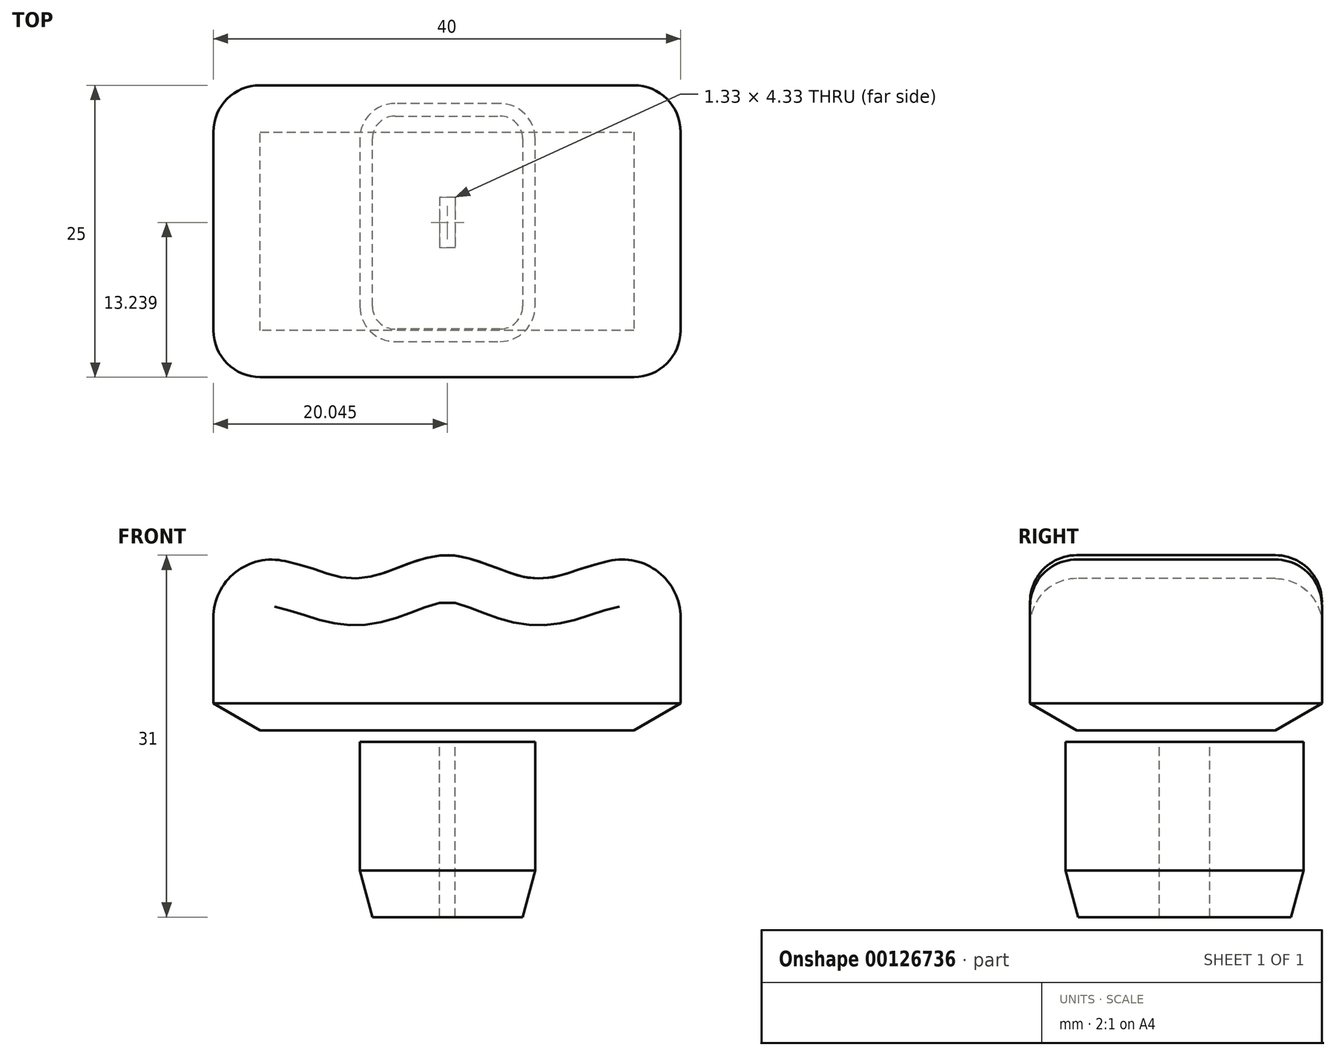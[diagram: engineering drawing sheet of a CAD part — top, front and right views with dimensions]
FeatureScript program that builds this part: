
annotation { "Feature Type Name" : "Feature", "Feature Type Description" : "" }
export const myFeature = defineFeature(function(context is Context, id is Id, definition is map)
    precondition{}
    {
        {
            var Q0;
            Q0=qCreatedBy(makeId("Front.planeOp"),FACE);
            var sketch = newSketch(context, id + "F0", { "sketchPlane" : qUnion([Q0])});
            skPoint(sketch, "E0.MirrorCS.start.orphan", {"position": v(0, 0) * mm});
            skPoint(sketch, "E1.MirrorCS.end.orphan", {"position": v(-8, 0) * mm});
            skPoint(sketch, "E2.MirrorCS.end.orphan", {"position": v(-24, 0) * mm});
            skPoint(sketch, "E2.MirrorCS.start.orphan", {"position": v(-16, 0) * mm});
            skPoint(sketch, "E3.MirrorCS.end.orphan", {"position": v(24, 0) * mm});
            skLineSegment(sketch, "E4", {"start": v(-24, 0) * mm, "end": v(-24, -14) * mm});
            skLineSegment(sketch, "E5", {"start": v(-24, -14) * mm, "end": v(16, -14) * mm});
            skLineSegment(sketch, "E6", {"start": v(16, -14) * mm, "end": v(16, 0) * mm});
            skPoint(sketch, "E7.MirrorCS.end.orphan", {"position": v(8, 0) * mm});
            skLineSegment(sketch, "E8", {"start": v(-24, 0) * mm, "end": v(-16, 0) * mm, "construction": true});
            skLineSegment(sketch, "E9", {"start": v(-16, 0) * mm, "end": v(-8, 0) * mm, "construction": true});
            skLineSegment(sketch, "E10", {"start": v(-8, 0) * mm, "end": v(0, 0) * mm, "construction": true});
            skLineSegment(sketch, "E11", {"start": v(0, 0) * mm, "end": v(8, 0) * mm, "construction": true});
            skLineSegment(sketch, "E12", {"start": v(8, 0) * mm, "end": v(16, 0) * mm, "construction": true});
            skLineSegment(sketch, "E13", {"start": v(-20, 0) * mm, "end": v(-20, 1) * mm, "construction": true});
            skLineSegment(sketch, "E14", {"start": v(-12, 0) * mm, "end": v(-12, -1) * mm, "construction": true});
            skLineSegment(sketch, "E15", {"start": v(-4, 0) * mm, "end": v(-4, 1) * mm, "construction": true});
            skLineSegment(sketch, "E16", {"start": v(4, 0) * mm, "end": v(4, -1) * mm, "construction": true});
            skPoint(sketch, "E16.endSnap0", {"position": v(4, 0) * mm});
            skLineSegment(sketch, "E17", {"start": v(12, 0) * mm, "end": v(12, 1) * mm, "construction": true});
            skFitSpline(sketch, "E18", {"points": [v(-24, 0) * mm, v(-20, 1) * mm, v(-16, 0) * mm, v(-12, -1) * mm, v(-8, 0) * mm, v(-4, 1) * mm, v(0, 0) * mm, v(4, -1) * mm, v(8, 0) * mm, v(12, 1) * mm, v(16, 0) * mm], "startDerivative": vector(5.73, 62.47) * mm, "endDerivative": vector(6.75, -59.62) * mm});
            skSolve(sketch);
        }
        {
            var Q0;
            Q0=makeQuery(id+"F0.imprint","IMPRINT",FACE,{"disambiguationData":[TD([[makeQuery(id+"F0.imprint","IMPRINT",EDGE,{"derivedFrom":sQuery(id+"F0.wireOp",EDGE,"E4")}),1.0]])]});
            extrude(context, id + "F1", {"entities" : qUnion([Q0]), "depth" : 25 * mm});
        }
        {
            var Q0;
            Q0=makeQuery(id+"F1.opExtrude","SWEPT_EDGE",EDGE,{"disambiguationData":[OSD([sQuery(id+"F0.wireOp",EDGE,"E4"),sQuery(id+"F0.wireOp",EDGE,"E18")])]});
            var Q1;
            Q1=makeQuery(id+"F1.opExtrude","SWEPT_EDGE",EDGE,{"disambiguationData":[OSD([sQuery(id+"F0.wireOp",EDGE,"E6"),sQuery(id+"F0.wireOp",EDGE,"E18")])]});
            fillet(context, id + "F2", {"entities" : qUnion([Q0, Q1]), "radius" : 5 * mm, "tangentPropagation" : true, "allowEdgeOverflow" : false});
        }
        {
            var Q0;
            Q0=makeQuery(id+"F1.opExtrude","CAP_EDGE",EDGE,{"disambiguationData":[OSD([sQuery(id+"F0.wireOp",EDGE,"E18")])],"isStart":false});
            var Q1;
            {var subQ0=sQuery(id+"F0.wireOp",EDGE,"E18");var subQ1=sQuery(id+"F0.wireOp",EDGE,"E4");Q1=makeQuery(id+"F2.opFillet","BLEND_EDGE",EDGE,{"blendedFrom":[makeQuery(id+"F1.opExtrude","SWEPT_EDGE",EDGE,{"disambiguationData":[OSD([subQ1,subQ0])]}),makeQuery(id+"F1.opExtrude","CAP_FACE",FACE,{"disambiguationData":[OSD([subQ1,sQuery(id+"F0.wireOp",EDGE,"E5"),sQuery(id+"F0.wireOp",EDGE,"E6"),subQ0])],"isStart":false})],"blendedInto":[makeQuery(id+"F1.opExtrude","CAP_FACE",FACE,{"disambiguationData":[OSD([subQ1,sQuery(id+"F0.wireOp",EDGE,"E5"),sQuery(id+"F0.wireOp",EDGE,"E6"),subQ0])],"isStart":false})]});}
            var Q2;
            {var subQ0=sQuery(id+"F0.wireOp",EDGE,"E18");var subQ1=sQuery(id+"F0.wireOp",EDGE,"E6");Q2=makeQuery(id+"F2.opFillet","BLEND_EDGE",EDGE,{"blendedFrom":[makeQuery(id+"F1.opExtrude","SWEPT_EDGE",EDGE,{"disambiguationData":[OSD([subQ1,subQ0])]}),makeQuery(id+"F1.opExtrude","CAP_FACE",FACE,{"disambiguationData":[OSD([sQuery(id+"F0.wireOp",EDGE,"E4"),sQuery(id+"F0.wireOp",EDGE,"E5"),subQ1,subQ0])],"isStart":false})],"blendedInto":[makeQuery(id+"F1.opExtrude","CAP_FACE",FACE,{"disambiguationData":[OSD([sQuery(id+"F0.wireOp",EDGE,"E4"),sQuery(id+"F0.wireOp",EDGE,"E5"),subQ1,subQ0])],"isStart":false})]});}
            fillet(context, id + "F3", {"entities" : qUnion([Q0, Q1, Q2]), "radius" : 4 * mm, "tangentPropagation" : true, "allowEdgeOverflow" : false});
        }
        {
            var Q0;
            Q0=makeQuery(id+"F1.opExtrude","CAP_EDGE",EDGE,{"disambiguationData":[OSD([sQuery(id+"F0.wireOp",EDGE,"E18")])],"isStart":true});
            var Q1;
            {var subQ0=sQuery(id+"F0.wireOp",EDGE,"E18");var subQ1=sQuery(id+"F0.wireOp",EDGE,"E4");Q1=makeQuery(id+"F2.opFillet","BLEND_EDGE",EDGE,{"blendedFrom":[makeQuery(id+"F1.opExtrude","SWEPT_EDGE",EDGE,{"disambiguationData":[OSD([subQ1,subQ0])]}),makeQuery(id+"F1.opExtrude","CAP_FACE",FACE,{"disambiguationData":[OSD([subQ1,sQuery(id+"F0.wireOp",EDGE,"E5"),sQuery(id+"F0.wireOp",EDGE,"E6"),subQ0])],"isStart":true})],"blendedInto":[makeQuery(id+"F1.opExtrude","CAP_FACE",FACE,{"disambiguationData":[OSD([subQ1,sQuery(id+"F0.wireOp",EDGE,"E5"),sQuery(id+"F0.wireOp",EDGE,"E6"),subQ0])],"isStart":true})]});}
            var Q2;
            Q2=makeQuery(id+"F1.opExtrude","CAP_EDGE",EDGE,{"disambiguationData":[OSD([sQuery(id+"F0.wireOp",EDGE,"E4")])],"isStart":true});
            var Q3;
            {var subQ0=sQuery(id+"F0.wireOp",EDGE,"E18");var subQ1=sQuery(id+"F0.wireOp",EDGE,"E6");Q3=makeQuery(id+"F2.opFillet","BLEND_EDGE",EDGE,{"blendedFrom":[makeQuery(id+"F1.opExtrude","SWEPT_EDGE",EDGE,{"disambiguationData":[OSD([subQ1,subQ0])]}),makeQuery(id+"F1.opExtrude","CAP_FACE",FACE,{"disambiguationData":[OSD([sQuery(id+"F0.wireOp",EDGE,"E4"),sQuery(id+"F0.wireOp",EDGE,"E5"),subQ1,subQ0])],"isStart":true})],"blendedInto":[makeQuery(id+"F1.opExtrude","CAP_FACE",FACE,{"disambiguationData":[OSD([sQuery(id+"F0.wireOp",EDGE,"E4"),sQuery(id+"F0.wireOp",EDGE,"E5"),subQ1,subQ0])],"isStart":true})]});}
            var Q4;
            Q4=makeQuery(id+"F1.opExtrude","CAP_EDGE",EDGE,{"disambiguationData":[OSD([sQuery(id+"F0.wireOp",EDGE,"E6")])],"isStart":true});
            fillet(context, id + "F4", {"entities" : qUnion([Q0, Q1, Q2, Q3, Q4]), "radius" : 4 * mm, "tangentPropagation" : true, "allowEdgeOverflow" : false});
        }
        {
            var Q0;
            Q0=makeQuery(id+"F1.opExtrude","SWEPT_FACE",FACE,{"disambiguationData":[OSD([sQuery(id+"F0.wireOp",EDGE,"E5")])]});
            chamfer(context, id + "F5", {"entities" : qUnion([Q0]), "chamferType" : ChamferType.OFFSET_ANGLE, "width" : 4 * mm, "oppositeDirection" : false, "angle" : 30 * degree, "tangentPropagation" : true});
        }
        {
            var Q0;
            Q0=makeQuery(id+"F1.opExtrude","SWEPT_FACE",FACE,{"disambiguationData":[OSD([sQuery(id+"F0.wireOp",EDGE,"E5")])]});
            cPlane(context, id + "F6", {"entities" : qUnion([Q0]), "cplaneType" : CPlaneType.OFFSET, "offset" : 1 * mm, "width" : 150 * mm, "height" : 150 * mm});
        }
        {
            var Q0;
            Q0=qCreatedBy(id+"F6.planeOp",FACE);
            var sketch = newSketch(context, id + "F7", { "sketchPlane" : qUnion([Q0])});
            skPoint(sketch, "E19.0.7.end.orphan", {"position": v(-21.7, 4) * mm});
            skPoint(sketch, "E19.0.6.end.orphan", {"position": v(-21.7, 21) * mm});
            skPoint(sketch, "E19.0.3.end.orphan", {"position": v(13.7, 21) * mm});
            skPoint(sketch, "E19.0.2.end.orphan", {"position": v(13.7, 4) * mm});
            skPoint(sketch, "E20", {"position": v(-3.96, 1.57) * mm});
            skPoint(sketch, "E21", {"position": v(-3.96, 21.95) * mm});
            skLineSegment(sketch, "E22", {"start": v(-3.96, 1.57) * mm, "end": v(-8.46, 1.57) * mm});
            skLineSegment(sketch, "E23", {"start": v(-11.46, 4.57) * mm, "end": v(-11.46, 18.95) * mm});
            skLineSegment(sketch, "E24", {"start": v(-8.46, 21.95) * mm, "end": v(-3.96, 21.95) * mm});
            skLineSegment(sketch, "E25", {"start": v(3.54, 18.95) * mm, "end": v(3.54, 4.57) * mm});
            skLineSegment(sketch, "E26", {"start": v(0.54, 1.57) * mm, "end": v(-3.96, 1.57) * mm});
            skLineSegment(sketch, "E27", {"start": v(-3.96, 21.95) * mm, "end": v(0.54, 21.95) * mm});
            skPoint(sketch, "E28.visualSharp", {"position": v(3.54, 1.57) * mm});
            skArc(sketch, "E28.filletArc", {"start": v(0.54, 1.57) * mm, "mid": v(2.67, 2.45) * mm, "end": v(3.54, 4.57) * mm});
            skPoint(sketch, "E29.visualSharp", {"position": v(-11.46, 1.57) * mm});
            skArc(sketch, "E29.filletArc", {"start": v(-11.46, 4.57) * mm, "mid": v(-10.58, 2.45) * mm, "end": v(-8.46, 1.57) * mm});
            skPoint(sketch, "E30.visualSharp", {"position": v(-11.46, 21.95) * mm});
            skArc(sketch, "E30.filletArc", {"start": v(-8.46, 21.95) * mm, "mid": v(-10.58, 21.07) * mm, "end": v(-11.46, 18.95) * mm});
            skPoint(sketch, "E31.visualSharp", {"position": v(3.54, 21.95) * mm});
            skArc(sketch, "E31.filletArc", {"start": v(3.54, 18.95) * mm, "mid": v(2.67, 21.07) * mm, "end": v(0.54, 21.95) * mm});
            skLineSegment(sketch, "E32", {"start": v(-3.96, 1.57) * mm, "end": v(-3.96, 21.95) * mm, "construction": true});
            skPoint(sketch, "E33", {"position": v(-3.96, 11.76) * mm});
            skLineSegment(sketch, "E34.bottom", {"start": v(-3.3, 9.6) * mm, "end": v(-4.62, 9.6) * mm});
            skLineSegment(sketch, "E34.top", {"start": v(-3.3, 13.93) * mm, "end": v(-4.62, 13.93) * mm});
            skLineSegment(sketch, "E34.left", {"start": v(-3.3, 9.6) * mm, "end": v(-3.3, 13.93) * mm});
            skLineSegment(sketch, "E34.right", {"start": v(-4.62, 9.6) * mm, "end": v(-4.62, 13.93) * mm});
            skSolve(sketch);
        }
        {
            var Q0;
            Q0=makeQuery(id+"F7.imprint","IMPRINT",FACE,{"disambiguationData":[TD([[makeQuery(id+"F7.imprint","IMPRINT",EDGE,{"derivedFrom":sQuery(id+"F7.wireOp",EDGE,"E22")}),-1.0]])]});
            extrude(context, id + "F8", {"entities" : qUnion([Q0]), "depth" : 15 * mm});
        }
        {
            var Q0;
            Q0=makeQuery(id+"F8.opExtrude","CAP_EDGE",EDGE,{"disambiguationData":[OSD([sQuery(id+"F7.wireOp",EDGE,"E25")])],"isStart":false});
            var Q1;
            Q1=makeQuery(id+"F8.opExtrude","CAP_EDGE",EDGE,{"disambiguationData":[OSD([sQuery(id+"F7.wireOp",EDGE,"E23")])],"isStart":false});
            chamfer(context, id + "F9", {"entities" : qUnion([Q0, Q1]), "chamferType" : ChamferType.OFFSET_ANGLE, "width" : 4 * mm, "oppositeDirection" : false, "angle" : 15 * degree, "tangentPropagation" : true});
        }
    });
